# Revit family: Stex 45 Montageplatte MP
name_source: partatom
category: HLS-Bauteile
revit_build: Autodesk Revit 2017 (Build: 20190507_1515(x64)
units: mm (PartAtom-declared; Revit-internal decimal feet)

## family parameters
Arbeitsebenenbasiert = Ja
Beim Laden mit Abzugskörper schneiden = Nein
Bemaßung runder Anschluss = Durchmesser verwenden
Gemeinsam genutzt = Ja
Immer vertikal = Nein
Raumberechnungspunkt = Nein
Teiletyp = Normal

## types (4) — shared parameters
Anzugsmoment = 0.00 kN-m
Fabrikat = MEFA
Firma = MEFA Befestigungs- und Montagesysteme GmbH
Kurztext1 = Stex Montageplatte MP 45
Material = Stahl
Mengeneinheit = St
Oberflaeche = galvanisch verzinkt
Profiltyp = 45
Vorgabe-Ansicht = 1219 mm
vpe = 30 St
zero-valued in all types: Länge Gewinde

## per-type parameters (varying)
| type | Artikelnummer | EAN | Gewicht | Gewicht pro Bauteil | Gewinde | Kurztext2 | Zahnplatte Gewinde |
| Stex 45 Montageplatte MP M 8 | 1280008 | 4250928424679 | 0.06 kg | 0.06 kg | M8 | M8 gvz | MEFA Zahnplatte 34x21 für Stex 45 : MEFA Zahnplatte 34x21 für Stex 45 M 8 |
| Stex 45 Montageplatte MP M10 | 1280010 | 4250928424686 | 0.06 kg | 0.06 kg | M10 | M10 gvz | MEFA Zahnplatte 34x21 für Stex 45 : MEFA Zahnplatte 34x21 für Stex 45 M10 |
| Stex 45 Montageplatte MP M12 | 1280012 | 4250928424693 | 0.05 kg | 0.05 kg | M12 | M12 gvz | MEFA Zahnplatte 34x21 für Stex 45 : MEFA Zahnplatte 34x21 für Stex 45 M12 |
| Stex 45 Montageplatte MP M 6 | 1280006 | 4250928424662 | 0.06 kg | 0.06 kg | M6 | M6 gvz | MEFA Zahnplatte 34x21 für Stex 45 : MEFA Zahnplatte 34x21 für Stex 45 M 6 |
